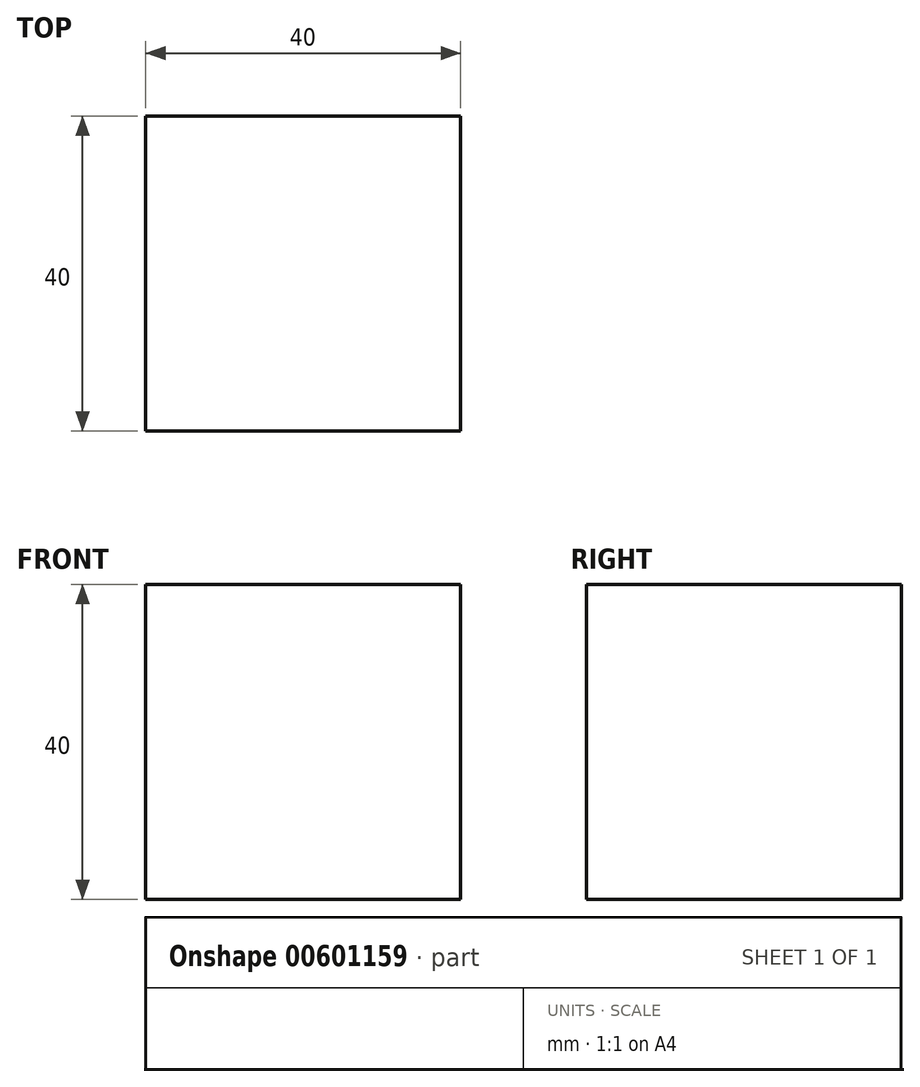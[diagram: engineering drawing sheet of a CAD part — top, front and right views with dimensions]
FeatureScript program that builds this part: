
annotation { "Feature Type Name" : "Feature", "Feature Type Description" : "" }
export const myFeature = defineFeature(function(context is Context, id is Id, definition is map)
    precondition{}
    {
        {
            var Q0;
            Q0=qCreatedBy(makeId("Top.planeOp"),FACE);
            var sketch = newSketch(context, id + "F0", { "sketchPlane" : qUnion([Q0])});
            skLineSegment(sketch, "E0.bottom", {"start": v(20, -20) * mm, "end": v(-20, -20) * mm});
            skLineSegment(sketch, "E0.top", {"start": v(20, 20) * mm, "end": v(-20, 20) * mm});
            skLineSegment(sketch, "E0.left", {"start": v(20, -20) * mm, "end": v(20, 20) * mm});
            skLineSegment(sketch, "E0.right", {"start": v(-20, -20) * mm, "end": v(-20, 20) * mm});
            skPoint(sketch, "E0.middle", {"position": v(0, 0) * mm});
            skSolve(sketch);
        }
        {
            var Q0;
            Q0 = qSketchRegion(id + "F0", true);
            var Q1;
            Q1=makeQuery(id+"F0.imprint","IMPRINT",FACE,{"disambiguationData":[TD([[makeQuery(id+"F0.imprint","IMPRINT",EDGE,{"derivedFrom":sQuery(id+"F0.wireOp",EDGE,"E0.bottom")}),-1.0]])]});
            extrude(context, id + "F1", {"entities" : qUnion([Q0, Q1]), "depth" : 40 * mm, "offsetDistance" : 25 * mm});
        }
    });
